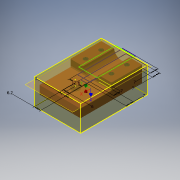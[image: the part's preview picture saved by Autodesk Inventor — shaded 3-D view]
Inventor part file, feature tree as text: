
AUTODESK INVENTOR PART (.ipt)
format: ipt  version: 2016 SP2 (Build 200236200, 236)  size: 654,848 bytes
history: native  units: mm
features: sketch x8, extrude x3, hole x3, plane x2, chamfer x1, projected_geometry x1
ambient origin geometry x8: Origin, YZ Plane, XZ Plane, XY Plane, X Axis, Y Axis, Z Axis, Center Point
bodies: Solid1 (feature_tree)
feature tree (18):
  extrude  "Extrusion1"  Depth=40.0mm
  hole  "Hole1"  [1 undecoded]
  extrude  "Extrusion2"  Depth=30.0mm
  extrude  "Extrusion3"  Depth=7.0mm
  hole  "Hole3"  [1 undecoded]
  plane  "Work Plane1"
  sketch  "Sketch6"  dims[d19=4.134mm d20=17.2mm d21=4.0mm d22=2.0mm d23=90.0deg d24=19.7mm d25=120.0deg]
  plane  "Work Plane2"
  sketch  "Sketch7"  dims[d26=-2.8mm]
  sketch  "Sketch8"  dims[d27=12.4mm d28=6.2mm d29=7.0mm d30=7.0mm d31=-5.5mm d32=6.0mm d33=7.0mm d35=7.0mm d36=3.0mm d37=0.25mm d38=2.0mm d39=45.0deg]
  chamfer  "Chamfer1"  Distance=6.2mm
  sketch  "Sketch1"  dims[d0=60.0mm d1=40.0mm]
  sketch  "Sketch2"  dims[d2=15.0mm d3=8.0mm d4=0.0mm]
  sketch  "Sketch3"  dims[d5=8.0mm d6=6.0mm d7=4.0mm d8=2.0mm d9=90.0deg d10=8.0mm d11=20.594885mm d12=30.0mm]
  projected_geometry  "Projected Loop1"
  sketch  "Sketch4"  dims[d13=7.0mm d14=0.0mm d15=1.0mm]
  sketch  "Sketch5"  dims[d16=15.0mm d17=7.0mm d18=0.0mm]
  hole  "Hole2"  [1 undecoded]
note: 3 required parameter values undecoded (feature->parameter linkage not recoverable at this tier; creation-order binding heuristic only, values carry confidence <= 0.55)
